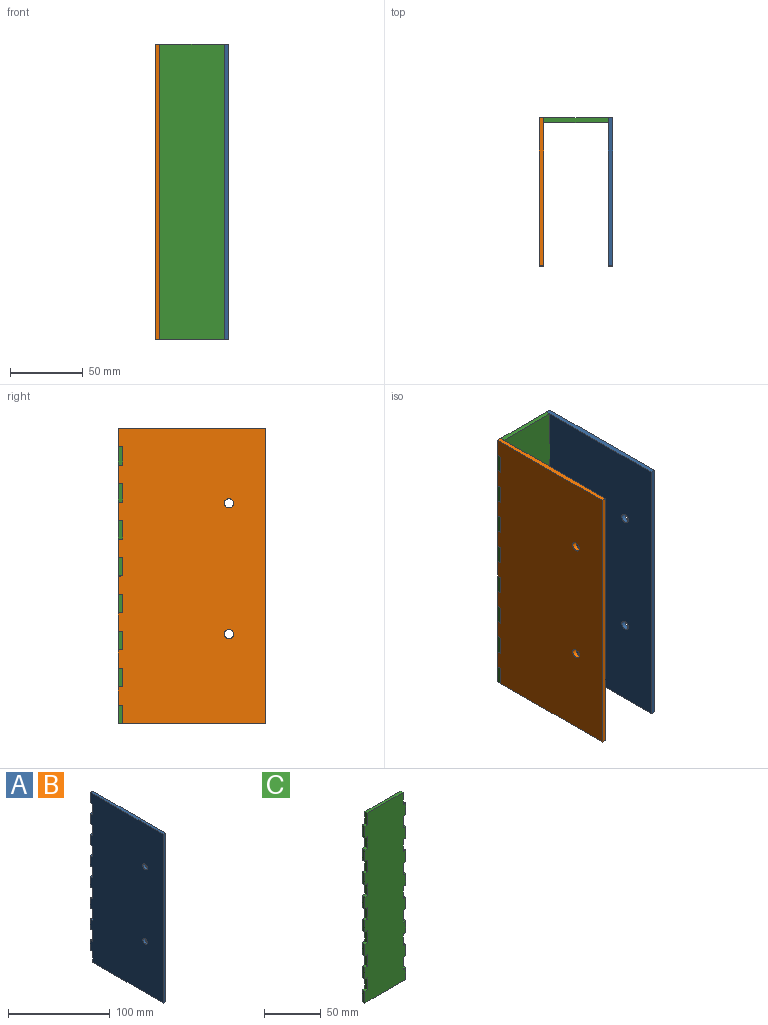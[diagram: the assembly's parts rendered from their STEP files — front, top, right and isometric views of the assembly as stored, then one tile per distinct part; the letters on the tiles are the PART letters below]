
ASSEMBLY  parts=3 mates=3
PART A: 38 faces, bbox 3.2x101.6x203.2 mm
  f0: plane 3.18x3.18mm, normal (0,0,-1), area 10.1mm2, adj f1,f35,f36,f37
  f1: plane 12.7x3.18mm, normal (0,1,0), area 40.3mm2, adj f0,f2,f36,f37
  f2: plane 3.18x3.18mm, normal (0,0,1), area 10.1mm2, adj f1,f3,f36,f37
  f3: plane 12.7x3.18mm, normal (0,1,0), area 40.3mm2, adj f2,f4,f36,f37
  f4: plane 3.18x3.18mm, normal (0,0,-1), area 10.1mm2, adj f3,f5,f36,f37
  f5: plane 12.7x3.18mm, normal (0,1,0), area 40.3mm2, adj f4,f6,f36,f37
  f6: plane 3.18x3.18mm, normal (0,0,1), area 10.1mm2, adj f5,f7,f36,f37
  f7: plane 12.7x3.18mm, normal (0,1,0), area 40.3mm2, adj f6,f8,f36,f37
  f8: plane 3.18x3.18mm, normal (0,0,-1), area 10.1mm2, adj f7,f9,f36,f37
  f9: plane 12.7x3.18mm, normal (0,1,0), area 40.3mm2, adj f8,f10,f36,f37
  f10: plane 3.18x3.18mm, normal (0,0,1), area 10.1mm2, adj f9,f11,f36,f37
  f11: plane 12.7x3.18mm, normal (0,1,0), area 40.3mm2, adj f10,f12,f36,f37
  f12: plane 3.18x3.18mm, normal (0,0,-1), area 10.1mm2, adj f11,f13,f36,f37
  f13: plane 12.7x3.18mm, normal (0,1,0), area 40.3mm2, adj f12,f14,f36,f37
  f14: plane 3.18x3.18mm, normal (0,0,1), area 10.1mm2, adj f13,f15,f36,f37
  f15: plane 12.7x3.18mm, normal (0,1,0), area 40.3mm2, adj f14,f16,f36,f37
  f16: plane 3.18x3.18mm, normal (0,0,-1), area 10.1mm2, adj f15,f17,f36,f37
  f17: plane 12.7x3.18mm, normal (0,1,0), area 40.3mm2, adj f16,f18,f36,f37
  f18: plane 3.18x3.18mm, normal (0,0,1), area 10.1mm2, adj f17,f19,f36,f37
  f19: plane 12.7x3.18mm, normal (0,1,0), area 40.3mm2, adj f18,f20,f36,f37
  f20: plane 3.18x3.18mm, normal (0,0,-1), area 10.1mm2, adj f19,f21,f36,f37
  f21: plane 12.7x3.18mm, normal (0,1,0), area 40.3mm2, adj f20,f22,f36,f37
  f22: plane 3.18x3.18mm, normal (0,0,1), area 10.1mm2, adj f21,f23,f36,f37
  f23: plane 12.7x3.18mm, normal (0,1,0), area 40.3mm2, adj f22,f24,f36,f37
  f24: plane 3.18x3.18mm, normal (0,0,-1), area 10.1mm2, adj f23,f25,f36,f37
  f25: plane 12.7x3.18mm, normal (0,1,0), area 40.3mm2, adj f24,f26,f36,f37
  f26: plane 3.18x3.18mm, normal (0,0,1), area 10.1mm2, adj f25,f27,f36,f37
  f27: plane 12.7x3.18mm, normal (0,1,0), area 40.3mm2, adj f26,f28,f36,f37
  f28: plane 3.18x3.18mm, normal (0,0,-1), area 10.1mm2, adj f27,f29,f36,f37
  f29: plane 12.7x3.18mm, normal (0,1,0), area 40.3mm2, adj f28,f30,f36,f37
  f30: plane 101.6x3.18mm, normal (0,0,1), area 322.6mm2, adj f29,f31,f36,f37
  f31: plane 203.2x3.18mm, normal (0,-1,0), area 645.2mm2, adj f30,f32,f36,f37
  f32: plane 98.43x3.18mm, normal (0,0,-1), area 312.5mm2, adj f31,f35,f36,f37
  f33: cylinder r=3.17mm len=6.35mm, axis (-1,0,0), area 63.3mm2, adj f36,f37
  f34: cylinder r=3.17mm len=6.35mm, axis (-1,0,0), area 63.3mm2, adj f36,f37
  f35: plane 12.7x3.18mm, normal (0,1,0), area 40.3mm2, adj f0,f32,f36,f37
  f36: plane 203.2x101.6mm, normal (1,0,0), area 20259.2mm2, adj f0,f1,f2,f3,f4,f5,f6,f7
  f37: plane 203.2x101.6mm, normal (-1,0,0), area 20259.2mm2, adj f0,f1,f2,f3,f4,f5,f6,f7
PART B: same geometry as A
PART C: 66 faces, bbox 50.8x3.2x203.2 mm
  f0: plane 12.7x3.18mm, normal (1,0,0), area 40.3mm2, adj f1,f63,f64,f65
  f1: plane 44.45x3.18mm, normal (0,0,1), area 141.1mm2, adj f0,f2,f64,f65
  f2: plane 12.7x3.18mm, normal (-1,0,0), area 40.3mm2, adj f1,f3,f64,f65
  f3: plane 3.18x3.18mm, normal (0,0,1), area 10.1mm2, adj f2,f4,f64,f65
  f4: plane 12.7x3.18mm, normal (-1,0,0), area 40.3mm2, adj f3,f5,f64,f65
  f5: plane 3.18x3.18mm, normal (0,0,-1), area 10.1mm2, adj f4,f6,f64,f65
  f6: plane 12.7x3.18mm, normal (-1,0,0), area 40.3mm2, adj f5,f7,f64,f65
  f7: plane 3.18x3.18mm, normal (0,0,1), area 10.1mm2, adj f6,f8,f64,f65
  f8: plane 12.7x3.18mm, normal (-1,0,0), area 40.3mm2, adj f7,f9,f64,f65
  f9: plane 3.18x3.18mm, normal (0,0,-1), area 10.1mm2, adj f8,f10,f64,f65
  f10: plane 12.7x3.18mm, normal (-1,0,0), area 40.3mm2, adj f9,f11,f64,f65
  f11: plane 3.18x3.18mm, normal (0,0,1), area 10.1mm2, adj f10,f12,f64,f65
  f12: plane 12.7x3.18mm, normal (-1,0,0), area 40.3mm2, adj f11,f13,f64,f65
  f13: plane 3.18x3.18mm, normal (0,0,-1), area 10.1mm2, adj f12,f14,f64,f65
  f14: plane 12.7x3.18mm, normal (-1,0,0), area 40.3mm2, adj f13,f15,f64,f65
  f15: plane 3.18x3.18mm, normal (0,0,1), area 10.1mm2, adj f14,f16,f64,f65
  f16: plane 12.7x3.18mm, normal (-1,0,0), area 40.3mm2, adj f15,f17,f64,f65
  f17: plane 3.18x3.18mm, normal (0,0,-1), area 10.1mm2, adj f16,f18,f64,f65
  f18: plane 12.7x3.18mm, normal (-1,0,0), area 40.3mm2, adj f17,f19,f64,f65
  f19: plane 3.18x3.18mm, normal (0,0,1), area 10.1mm2, adj f18,f20,f64,f65
  f20: plane 12.7x3.18mm, normal (-1,0,0), area 40.3mm2, adj f19,f21,f64,f65
  f21: plane 3.18x3.18mm, normal (0,0,-1), area 10.1mm2, adj f20,f22,f64,f65
  f22: plane 12.7x3.18mm, normal (-1,0,0), area 40.3mm2, adj f21,f23,f64,f65
  f23: plane 3.18x3.18mm, normal (0,0,1), area 10.1mm2, adj f22,f24,f64,f65
  f24: plane 12.7x3.18mm, normal (-1,0,0), area 40.3mm2, adj f23,f25,f64,f65
  f25: plane 3.18x3.18mm, normal (0,0,-1), area 10.1mm2, adj f24,f26,f64,f65
  f26: plane 12.7x3.18mm, normal (-1,0,0), area 40.3mm2, adj f25,f27,f64,f65
  f27: plane 3.18x3.18mm, normal (0,0,1), area 10.1mm2, adj f26,f28,f64,f65
  f28: plane 12.7x3.18mm, normal (-1,0,0), area 40.3mm2, adj f27,f29,f64,f65
  f29: plane 3.18x3.18mm, normal (0,0,-1), area 10.1mm2, adj f28,f30,f64,f65
  f30: plane 12.7x3.18mm, normal (-1,0,0), area 40.3mm2, adj f29,f31,f64,f65
  f31: plane 3.18x3.18mm, normal (0,0,1), area 10.1mm2, adj f30,f32,f64,f65
  f32: plane 12.7x3.18mm, normal (-1,0,0), area 40.3mm2, adj f31,f33,f64,f65
  f33: plane 50.8x3.18mm, normal (0,0,-1), area 161.3mm2, adj f32,f34,f64,f65
  f34: plane 12.7x3.18mm, normal (1,0,0), area 40.3mm2, adj f33,f35,f64,f65
  f35: plane 3.18x3.18mm, normal (0,0,1), area 10.1mm2, adj f34,f36,f64,f65
  f36: plane 12.7x3.18mm, normal (1,0,0), area 40.3mm2, adj f35,f37,f64,f65
  f37: plane 3.18x3.18mm, normal (0,0,-1), area 10.1mm2, adj f36,f38,f64,f65
  f38: plane 12.7x3.18mm, normal (1,0,0), area 40.3mm2, adj f37,f39,f64,f65
  f39: plane 3.18x3.18mm, normal (0,0,1), area 10.1mm2, adj f38,f40,f64,f65
  f40: plane 12.7x3.18mm, normal (1,0,0), area 40.3mm2, adj f39,f41,f64,f65
  f41: plane 3.18x3.18mm, normal (0,0,-1), area 10.1mm2, adj f40,f42,f64,f65
  f42: plane 12.7x3.18mm, normal (1,0,0), area 40.3mm2, adj f41,f43,f64,f65
  f43: plane 3.18x3.18mm, normal (0,0,1), area 10.1mm2, adj f42,f44,f64,f65
  f44: plane 12.7x3.18mm, normal (1,0,0), area 40.3mm2, adj f43,f45,f64,f65
  f45: plane 3.18x3.18mm, normal (0,0,-1), area 10.1mm2, adj f44,f46,f64,f65
  f46: plane 12.7x3.18mm, normal (1,0,0), area 40.3mm2, adj f45,f47,f64,f65
  f47: plane 3.18x3.18mm, normal (0,0,1), area 10.1mm2, adj f46,f48,f64,f65
  f48: plane 12.7x3.18mm, normal (1,0,0), area 40.3mm2, adj f47,f49,f64,f65
  f49: plane 3.18x3.18mm, normal (0,0,-1), area 10.1mm2, adj f48,f50,f64,f65
  f50: plane 12.7x3.18mm, normal (1,0,0), area 40.3mm2, adj f49,f51,f64,f65
  f51: plane 3.18x3.18mm, normal (0,0,1), area 10.1mm2, adj f50,f52,f64,f65
  f52: plane 12.7x3.18mm, normal (1,0,0), area 40.3mm2, adj f51,f53,f64,f65
  f53: plane 3.18x3.18mm, normal (0,0,-1), area 10.1mm2, adj f52,f54,f64,f65
  f54: plane 12.7x3.18mm, normal (1,0,0), area 40.3mm2, adj f53,f55,f64,f65
  f55: plane 3.18x3.18mm, normal (0,0,1), area 10.1mm2, adj f54,f56,f64,f65
  f56: plane 12.7x3.18mm, normal (1,0,0), area 40.3mm2, adj f55,f57,f64,f65
  f57: plane 3.18x3.18mm, normal (0,0,-1), area 10.1mm2, adj f56,f58,f64,f65
  f58: plane 12.7x3.18mm, normal (1,0,0), area 40.3mm2, adj f57,f59,f64,f65
  f59: plane 3.18x3.18mm, normal (0,0,1), area 10.1mm2, adj f58,f60,f64,f65
  f60: plane 12.7x3.18mm, normal (1,0,0), area 40.3mm2, adj f59,f61,f64,f65
  f61: plane 3.18x3.18mm, normal (0,0,-1), area 10.1mm2, adj f60,f62,f64,f65
  f62: plane 12.7x3.18mm, normal (1,0,0), area 40.3mm2, adj f61,f63,f64,f65
  f63: plane 3.18x3.18mm, normal (0,0,1), area 10.1mm2, adj f0,f62,f64,f65
  f64: plane 203.2x50.8mm, normal (0,-1,0), area 9677.4mm2, adj f0,f1,f2,f3,f4,f5,f6,f7
  f65: plane 203.2x50.8mm, normal (0,1,0), area 9677.4mm2, adj f0,f1,f2,f3,f4,f5,f6,f7
PLACE A t=(-11.3,11.82,-2.09)mm
PLACE B t=(-58.92,11.82,-2.09)mm
PLACE C t=(-33.52,49.92,-2.09)mm
MATE fastened A.f37 <-> C.f0  axis (-1,0,0) through (-11.3,49.92,93.16)mm
MATE fastened C.f64 <-> B.f27  axis (0,-1,0) through (-58.92,46.74,80.46)mm
MATE fastened C.f2 <-> B.f36  axis (-1,0,0) through (-55.75,48.33,93.16)mm
